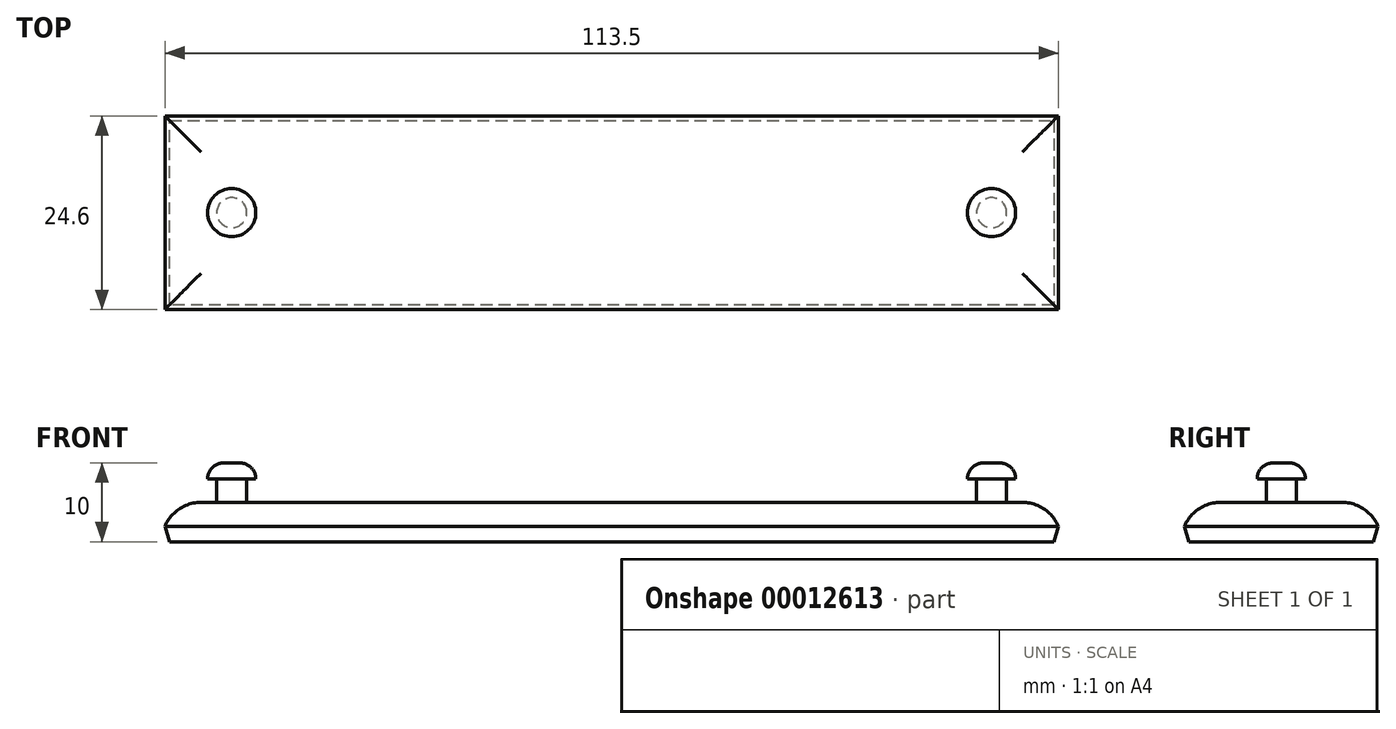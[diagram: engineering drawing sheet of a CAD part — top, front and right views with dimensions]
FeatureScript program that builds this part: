
annotation { "Feature Type Name" : "Feature", "Feature Type Description" : "" }
export const myFeature = defineFeature(function(context is Context, id is Id, definition is map)
    precondition{}
    {
        {
            var Q0;
            Q0=qCreatedBy(makeId("Top.planeOp"),FACE);
            var sketch = newSketch(context, id + "F0", { "sketchPlane" : qUnion([Q0])});
            skLineSegment(sketch, "E0.rect.bottom", {"start": v(57.15, 12.7) * mm, "end": v(-57.15, 12.7) * mm});
            skLineSegment(sketch, "E0.rect.top", {"start": v(57.15, -12.7) * mm, "end": v(-57.15, -12.7) * mm});
            skLineSegment(sketch, "E0.rect.left", {"start": v(57.15, 12.7) * mm, "end": v(57.15, -12.7) * mm});
            skLineSegment(sketch, "E0.rect.right", {"start": v(-57.15, 12.7) * mm, "end": v(-57.15, -12.7) * mm});
            skPoint(sketch, "E0.rect.middle", {"position": v(0, 0) * mm});
            skSolve(sketch);
        }
        {
            var Q0;
            Q0 = qSketchRegion(id + "F0", true);
            extrude(context, id + "F1", {"entities" : qUnion([Q0]), "depth" : 5 * mm});
        }
        {
            var Q0;
            Q0=makeQuery(id+"F1.opExtrude","CAP_FACE",FACE,{"disambiguationData":[OSD([sQuery(id+"F0.wireOp",EDGE,"E0.rect.bottom"),sQuery(id+"F0.wireOp",EDGE,"E0.rect.top"),sQuery(id+"F0.wireOp",EDGE,"E0.rect.left"),sQuery(id+"F0.wireOp",EDGE,"E0.rect.right")])],"isStart":false});
            fillet(context, id + "F2", {"entities" : qUnion([Q0]), "radius" : 5 * mm, "tangentPropagation" : true, "allowEdgeOverflow" : false});
        }
        {
            var Q0;
            Q0=makeQuery(id+"F1.opExtrude","CAP_FACE",FACE,{"disambiguationData":[OSD([sQuery(id+"F0.wireOp",EDGE,"E0.rect.bottom"),sQuery(id+"F0.wireOp",EDGE,"E0.rect.top"),sQuery(id+"F0.wireOp",EDGE,"E0.rect.left"),sQuery(id+"F0.wireOp",EDGE,"E0.rect.right")])],"isStart":false});
            var sketch = newSketch(context, id + "F3", { "sketchPlane" : qUnion([Q0])});
            skCircle(sketch, "E1", {"center": v(-48.26, 0) * mm, "radius": 1.9 * mm});
            skCircle(sketch, "E2.MirrorC", {"center": v(48.26, 0) * mm, "radius": 1.9 * mm});
            skSolve(sketch);
        }
        {
            var Q0;
            Q0 = qSketchRegion(id + "F3", true);
            extrude(context, id + "F4", {"entities" : qUnion([Q0]), "operationType" : NewBodyOperationType.ADD, "depth" : 3 * mm});
        }
        {
            var Q0;
            Q0=makeQuery(id+"F4.opExtrude","CAP_FACE",FACE,{"disambiguationData":[OSD([sQuery(id+"F3.wireOp",EDGE,"E1")])],"isStart":false});
            var sketch = newSketch(context, id + "F5", { "sketchPlane" : qUnion([Q0])});
            skCircle(sketch, "E3", {"center": v(-48.26, 0) * mm, "radius": 3.06 * mm});
            skCircle(sketch, "E4.MirrorC", {"center": v(48.26, 0) * mm, "radius": 3.06 * mm});
            skSolve(sketch);
        }
        {
            var Q0;
            Q0 = qSketchRegion(id + "F5", true);
            extrude(context, id + "F6", {"entities" : qUnion([Q0]), "operationType" : NewBodyOperationType.ADD, "depth" : 2 * mm});
        }
        {
            var Q0;
            Q0=makeQuery(id+"F6.opExtrude","CAP_FACE",FACE,{"disambiguationData":[OSD([sQuery(id+"F5.wireOp",EDGE,"E3")])],"isStart":false});
            var Q1;
            Q1=makeQuery(id+"F6.opExtrude","CAP_FACE",FACE,{"disambiguationData":[OSD([sQuery(id+"F5.wireOp",EDGE,"E4.MirrorC")])],"isStart":false});
            fillet(context, id + "F7", {"entities" : qUnion([Q0, Q1]), "radius" : 2 * mm, "tangentPropagation" : true, "allowEdgeOverflow" : false});
        }
        {
            var Q0;
            Q0=makeQuery(id+"F1.opExtrude","CAP_FACE",FACE,{"disambiguationData":[OSD([sQuery(id+"F0.wireOp",EDGE,"E0.rect.bottom"),sQuery(id+"F0.wireOp",EDGE,"E0.rect.top"),sQuery(id+"F0.wireOp",EDGE,"E0.rect.left"),sQuery(id+"F0.wireOp",EDGE,"E0.rect.right")])],"isStart":true});
            chamfer(context, id + "F8", {"entities" : qUnion([Q0]), "chamferType" : ChamferType.TWO_OFFSETS, "width1" : 1 * mm, "oppositeDirection" : false, "width2" : 2 * mm, "tangentPropagation" : true});
        }
    });
